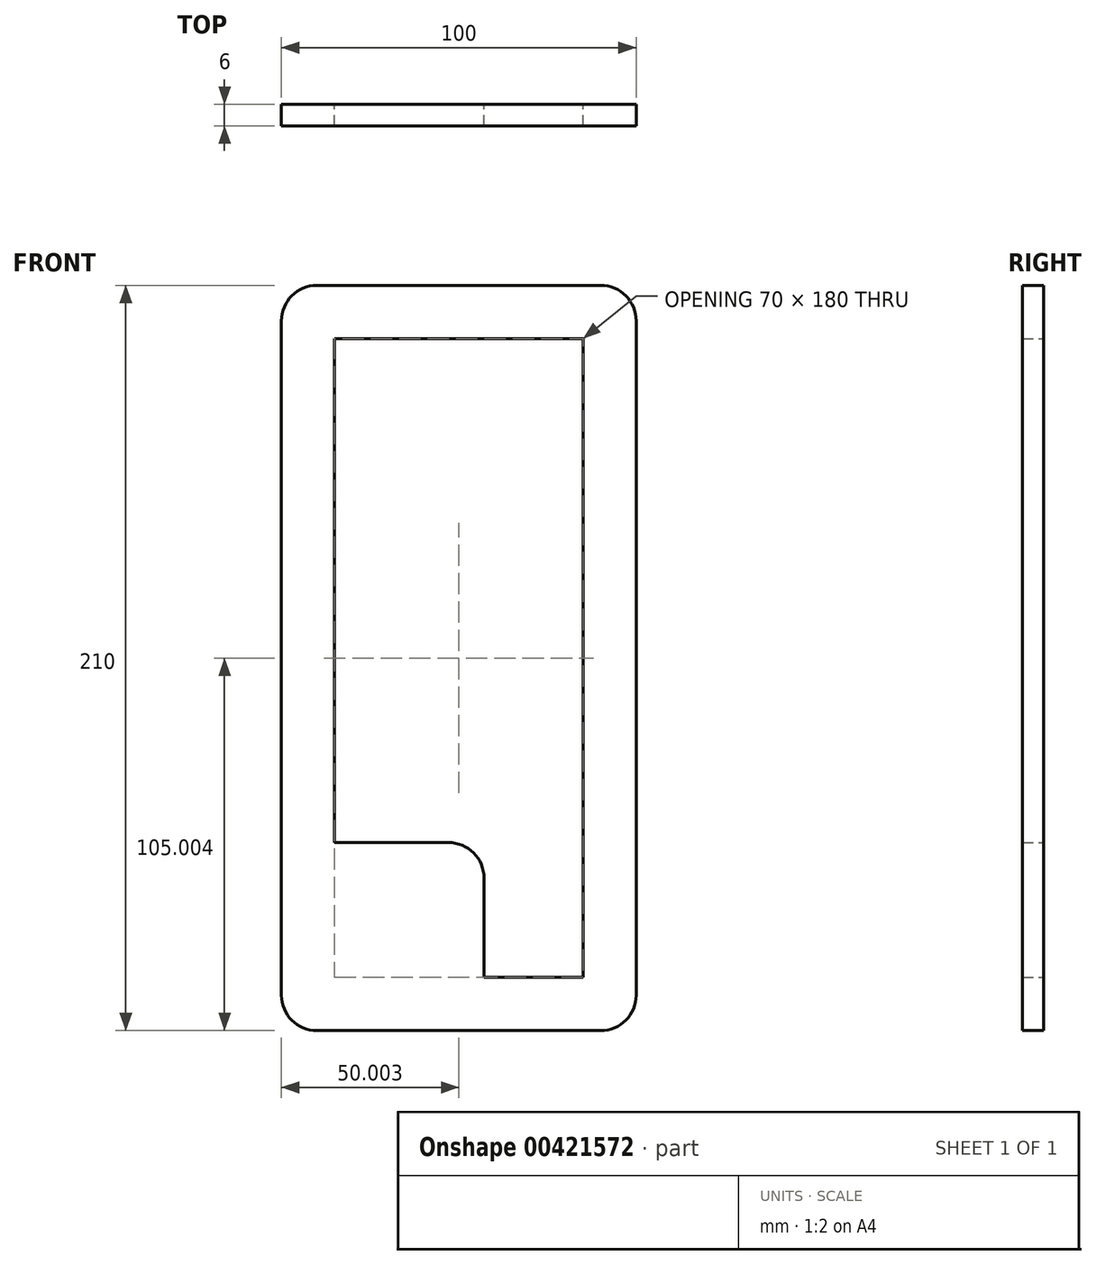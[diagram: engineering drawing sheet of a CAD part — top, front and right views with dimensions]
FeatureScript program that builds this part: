
annotation { "Feature Type Name" : "Feature", "Feature Type Description" : "" }
export const myFeature = defineFeature(function(context is Context, id is Id, definition is map)
    precondition{}
    {
        {
            var Q0;
            Q0=qCreatedBy(makeId("Front.planeOp"),FACE);
            var sketch = newSketch(context, id + "F0", { "sketchPlane" : qUnion([Q0])});
            skLineSegment(sketch, "E0.bottom", {"start": v(-46.45, 118.04) * mm, "end": v(23.55, 118.04) * mm});
            skLineSegment(sketch, "E0.top", {"start": v(-4.34, -61.96) * mm, "end": v(23.55, -61.96) * mm});
            skLineSegment(sketch, "E0.left", {"start": v(-46.45, 118.04) * mm, "end": v(-46.45, -23.96) * mm});
            skLineSegment(sketch, "E0.right", {"start": v(23.55, 118.04) * mm, "end": v(23.55, -61.96) * mm});
            skLineSegment(sketch, "E1.bottom", {"start": v(-51.45, 133.04) * mm, "end": v(28.55, 133.04) * mm});
            skLineSegment(sketch, "E1.top", {"start": v(-51.45, -76.96) * mm, "end": v(28.55, -76.96) * mm});
            skLineSegment(sketch, "E1.left", {"start": v(-61.45, 123.04) * mm, "end": v(-61.45, -66.96) * mm});
            skLineSegment(sketch, "E1.right", {"start": v(38.55, 123.04) * mm, "end": v(38.55, -66.96) * mm});
            skPoint(sketch, "E2.visualSharp", {"position": v(-61.45, 133.04) * mm});
            skArc(sketch, "E2.filletArc", {"start": v(-51.45, 133.04) * mm, "mid": v(-58.52, 130.11) * mm, "end": v(-61.45, 123.04) * mm});
            skPoint(sketch, "E3.visualSharp", {"position": v(38.55, 133.04) * mm});
            skArc(sketch, "E3.filletArc", {"start": v(38.55, 123.04) * mm, "mid": v(35.62, 130.11) * mm, "end": v(28.55, 133.04) * mm});
            skPoint(sketch, "E4.visualSharp", {"position": v(-61.45, -76.96) * mm});
            skArc(sketch, "E4.filletArc", {"start": v(-61.45, -66.96) * mm, "mid": v(-58.52, -74.03) * mm, "end": v(-51.45, -76.96) * mm});
            skPoint(sketch, "E5.visualSharp", {"position": v(38.55, -76.96) * mm});
            skArc(sketch, "E5.filletArc", {"start": v(28.55, -76.96) * mm, "mid": v(35.62, -74.03) * mm, "end": v(38.55, -66.96) * mm});
            skLineSegment(sketch, "E6.top", {"start": v(-46.45, -23.96) * mm, "end": v(-14.34, -23.96) * mm});
            skLineSegment(sketch, "E6.right", {"start": v(-4.34, -61.96) * mm, "end": v(-4.34, -33.96) * mm});
            skPoint(sketch, "E7.visualSharp", {"position": v(-4.34, -23.96) * mm});
            skArc(sketch, "E7.filletArc", {"start": v(-4.34, -33.96) * mm, "mid": v(-7.27, -26.89) * mm, "end": v(-14.34, -23.96) * mm});
            skSolve(sketch);
        }
        {
            var Q0;
            Q0 = qSketchRegion(id + "F0", true);
            extrude(context, id + "F1", {"entities" : qUnion([Q0]), "depth" : 6 * mm, "offsetDistance" : 25 * mm});
        }
    });
